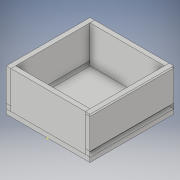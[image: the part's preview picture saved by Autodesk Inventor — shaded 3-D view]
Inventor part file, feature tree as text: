
AUTODESK INVENTOR PART (.ipt)
format: ipt  version: 2019 (Build 230136000, 136)  size: 193,024 bytes
history: native  units: mm
features: sketch x18, extrude x9, delete_face x6
ambient origin geometry x8: Origin, YZ Plane, XZ Plane, XY Plane, X Axis, Y Axis, Z Axis, Center Point
bodies: Solid1 (feature_tree), Solid2 (feature_tree), Solid3 (feature_tree)
feature tree (33):
  extrude  "Extrusion1"  Depth=90.0mm
  sketch  "Sketch2"  dims[d2=10.0mm d3=80.0mm]
  delete_face  "Delete Face1"
  delete_face  "Delete Face2"
  extrude  "Extrusion2"  Depth=80.0mm
  sketch  "Sketch4"  dims[d6=180.0mm d7=0.0mm d8=180.0mm d9=0.0mm]
  sketch  "Sketch5"  dims[d10=10.0mm d11=0.0mm d12=10.0mm d13=0.0mm]
  delete_face  "Delete Face3"
  delete_face  "Delete Face4"
  extrude  "Extrusion3"  Depth=10.0mm
  sketch  "Sketch7"  dims[d18=10.0mm d19=0.0mm d20=10.0mm d21=0.0mm]
  extrude  "Extrusion4"  Depth=180.0mm TaperAngle=0.0deg
  sketch  "3D Sketch1"
  extrude  "Extrusion5"  Depth=10.0mm TaperAngle=0.0deg
  sketch  "Sketch10"
  sketch  "Sketch11"
  extrude  "Extrusion6"  Depth=10.0mm TaperAngle=0.0deg
  sketch  "Sketch13"
  extrude  "Extrusion7"  Depth=10.0mm TaperAngle=0.0deg
  extrude  "Extrusion8"  [1 undecoded]
  delete_face  "Delete Face5"
  delete_face  "Delete Face6"
  sketch  "Sketch15"
  sketch  "Sketch16"
  extrude  "Extrusion9"  [1 undecoded]
  sketch  "Sketch1"  dims[d0=90.0mm d1=90.0mm]
  sketch  "Sketch3"  dims[d4=160.0mm d5=10.0mm]
  sketch  "Sketch6"  dims[d14=10.0mm d15=0.0mm d16=10.0mm d17=0.0mm]
  sketch  "Sketch8"  dims[d22=10.0mm d23=0.0mm]
  sketch  "Sketch9"
  sketch  "Sketch12"
  sketch  "Sketch14"
  sketch  "Sketch17"
note: 2 required parameter values undecoded (feature->parameter linkage not recoverable at this tier; creation-order binding heuristic only, values carry confidence <= 0.55)
